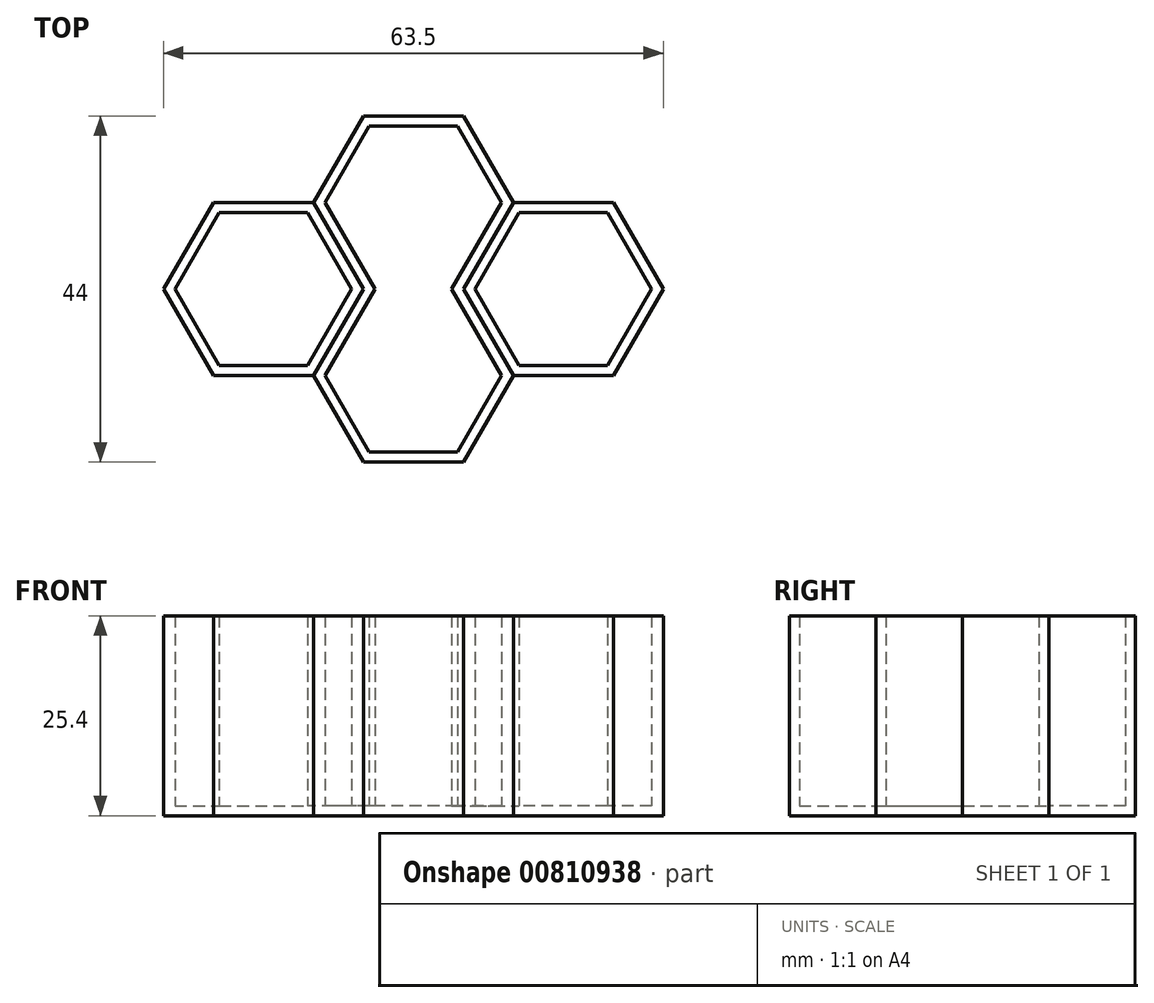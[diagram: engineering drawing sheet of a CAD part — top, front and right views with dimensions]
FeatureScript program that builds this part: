
annotation { "Feature Type Name" : "Feature", "Feature Type Description" : "" }
export const myFeature = defineFeature(function(context is Context, id is Id, definition is map)
    precondition{}
    {
        {
            var Q0;
            Q0=qCreatedBy(makeId("Top.planeOp"),FACE);
            var sketch = newSketch(context, id + "F0", { "sketchPlane" : qUnion([Q0])});
            skCircle(sketch, "E0.cCircle", {"center": v(0, 0) * mm, "radius": 11 * mm, "construction": true});
            skLineSegment(sketch, "E0.0", {"start": v(12.7, 0) * mm, "end": v(6.35, -11) * mm});
            skLineSegment(sketch, "E0.1", {"start": v(6.35, -11) * mm, "end": v(-6.35, -11) * mm});
            skLineSegment(sketch, "E0.2", {"start": v(-6.35, -11) * mm, "end": v(-12.7, 0) * mm});
            skLineSegment(sketch, "E0.3", {"start": v(-12.7, 0) * mm, "end": v(-6.35, 11) * mm});
            skLineSegment(sketch, "E0.4", {"start": v(-6.35, 11) * mm, "end": v(6.35, 11) * mm});
            skLineSegment(sketch, "E0.5", {"start": v(6.35, 11) * mm, "end": v(12.7, 0) * mm});
            skPoint(sketch, "E0.0.midPoint", {"position": v(9.53, -5.5) * mm});
            skCircle(sketch, "E1.cCircle", {"center": v(0, 22) * mm, "radius": 11 * mm, "construction": true});
            skLineSegment(sketch, "E1.0", {"start": v(12.7, 22) * mm, "end": v(6.35, 11) * mm});
            skLineSegment(sketch, "E1.1", {"start": v(6.35, 11) * mm, "end": v(-6.35, 11) * mm});
            skLineSegment(sketch, "E1.2", {"start": v(-6.35, 11) * mm, "end": v(-12.7, 22) * mm});
            skLineSegment(sketch, "E1.3", {"start": v(-12.7, 22) * mm, "end": v(-6.35, 33) * mm});
            skLineSegment(sketch, "E1.4", {"start": v(-6.35, 33) * mm, "end": v(6.35, 33) * mm});
            skLineSegment(sketch, "E1.5", {"start": v(6.35, 33) * mm, "end": v(12.7, 22) * mm});
            skPoint(sketch, "E1.0.midPoint", {"position": v(9.53, 16.5) * mm});
            skSolve(sketch);
        }
        {
            var Q0;
            Q0=qCreatedBy(makeId("Top.planeOp"),FACE);
            var sketch = newSketch(context, id + "F1", { "sketchPlane" : qUnion([Q0])});
            skCircle(sketch, "E2.cCircle", {"center": v(-19.05, 11) * mm, "radius": 11 * mm, "construction": true});
            skLineSegment(sketch, "E2.0", {"start": v(-25.4, 22) * mm, "end": v(-12.7, 22) * mm});
            skLineSegment(sketch, "E2.1", {"start": v(-12.7, 22) * mm, "end": v(-6.35, 11) * mm});
            skLineSegment(sketch, "E2.2", {"start": v(-6.35, 11) * mm, "end": v(-12.7, 0) * mm});
            skLineSegment(sketch, "E2.3", {"start": v(-12.7, 0) * mm, "end": v(-25.4, 0) * mm});
            skLineSegment(sketch, "E2.4", {"start": v(-25.4, 0) * mm, "end": v(-31.75, 11) * mm});
            skLineSegment(sketch, "E2.5", {"start": v(-31.75, 11) * mm, "end": v(-25.4, 22) * mm});
            skPoint(sketch, "E2.0.midPoint", {"position": v(-19.05, 22) * mm});
            skCircle(sketch, "E3.cCircle", {"center": v(19.05, 11) * mm, "radius": 11 * mm, "construction": true});
            skLineSegment(sketch, "E3.0", {"start": v(25.4, 0) * mm, "end": v(12.7, 0) * mm});
            skLineSegment(sketch, "E3.1", {"start": v(12.7, 0) * mm, "end": v(6.35, 11) * mm});
            skLineSegment(sketch, "E3.2", {"start": v(6.35, 11) * mm, "end": v(12.7, 22) * mm});
            skLineSegment(sketch, "E3.3", {"start": v(12.7, 22) * mm, "end": v(25.4, 22) * mm});
            skLineSegment(sketch, "E3.4", {"start": v(25.4, 22) * mm, "end": v(31.75, 11) * mm});
            skLineSegment(sketch, "E3.5", {"start": v(31.75, 11) * mm, "end": v(25.4, 0) * mm});
            skPoint(sketch, "E3.0.midPoint", {"position": v(19.05, 0) * mm});
            skSolve(sketch);
        }
        {
            var Q0;
            Q0=makeQuery(id+"F1.imprint","IMPRINT",FACE,{"disambiguationData":[TD([[makeQuery(id+"F1.imprint","IMPRINT",EDGE,{"derivedFrom":sQuery(id+"F1.wireOp",EDGE,"E2.0")}),-1.0]])]});
            var Q1;
            Q1=makeQuery(id+"F0.imprint","IMPRINT",FACE,{"disambiguationData":[TD([[makeQuery(id+"F0.imprint","IMPRINT",EDGE,{"derivedFrom":sQuery(id+"F0.wireOp",EDGE,"E1.0")}),-1.0]])]});
            var Q2;
            Q2=makeQuery(id+"F0.imprint","IMPRINT",FACE,{"disambiguationData":[TD([[makeQuery(id+"F0.imprint","IMPRINT",EDGE,{"derivedFrom":sQuery(id+"F0.wireOp",EDGE,"E0.0")}),-1.0]])]});
            var Q3;
            Q3=makeQuery(id+"F1.imprint","IMPRINT",FACE,{"disambiguationData":[TD([[makeQuery(id+"F1.imprint","IMPRINT",EDGE,{"derivedFrom":sQuery(id+"F1.wireOp",EDGE,"E3.0")}),-1.0]])]});
            extrude(context, id + "F2", {"entities" : qUnion([Q0, Q1, Q2, Q3]), "depth" : 25.4 * mm, "offsetDistance" : 25.4 * mm});
        }
        {
            var Q0;
            Q0=makeQuery(id+"F2.opExtrude","CAP_FACE",FACE,{"disambiguationData":[OSD([sQuery(id+"F0.wireOp",EDGE,"E0.0"),sQuery(id+"F0.wireOp",EDGE,"E0.1"),sQuery(id+"F0.wireOp",EDGE,"E0.2"),sQuery(id+"F0.wireOp",EDGE,"E0.3"),sQuery(id+"F0.wireOp",EDGE,"E0.5"),sQuery(id+"F0.wireOp",EDGE,"E1.0"),sQuery(id+"F0.wireOp",EDGE,"E1.2"),sQuery(id+"F0.wireOp",EDGE,"E1.3"),sQuery(id+"F0.wireOp",EDGE,"E1.4"),sQuery(id+"F0.wireOp",EDGE,"E1.5")])],"isStart":false});
            var Q1;
            Q1=makeQuery(id+"F2.opExtrude","CAP_FACE",FACE,{"disambiguationData":[OSD([sQuery(id+"F1.wireOp",EDGE,"E2.0"),sQuery(id+"F1.wireOp",EDGE,"E2.1"),sQuery(id+"F1.wireOp",EDGE,"E2.2"),sQuery(id+"F1.wireOp",EDGE,"E2.3"),sQuery(id+"F1.wireOp",EDGE,"E2.4"),sQuery(id+"F1.wireOp",EDGE,"E2.5")])],"isStart":false});
            var Q2;
            Q2=makeQuery(id+"F2.opExtrude","CAP_FACE",FACE,{"disambiguationData":[OSD([sQuery(id+"F1.wireOp",EDGE,"E3.0"),sQuery(id+"F1.wireOp",EDGE,"E3.1"),sQuery(id+"F1.wireOp",EDGE,"E3.2"),sQuery(id+"F1.wireOp",EDGE,"E3.3"),sQuery(id+"F1.wireOp",EDGE,"E3.4"),sQuery(id+"F1.wireOp",EDGE,"E3.5")])],"isStart":false});
            shell(context, id + "F3", {"entities" : qUnion([Q0, Q1, Q2]), "thickness" : 1.27 * mm});
        }
    });
